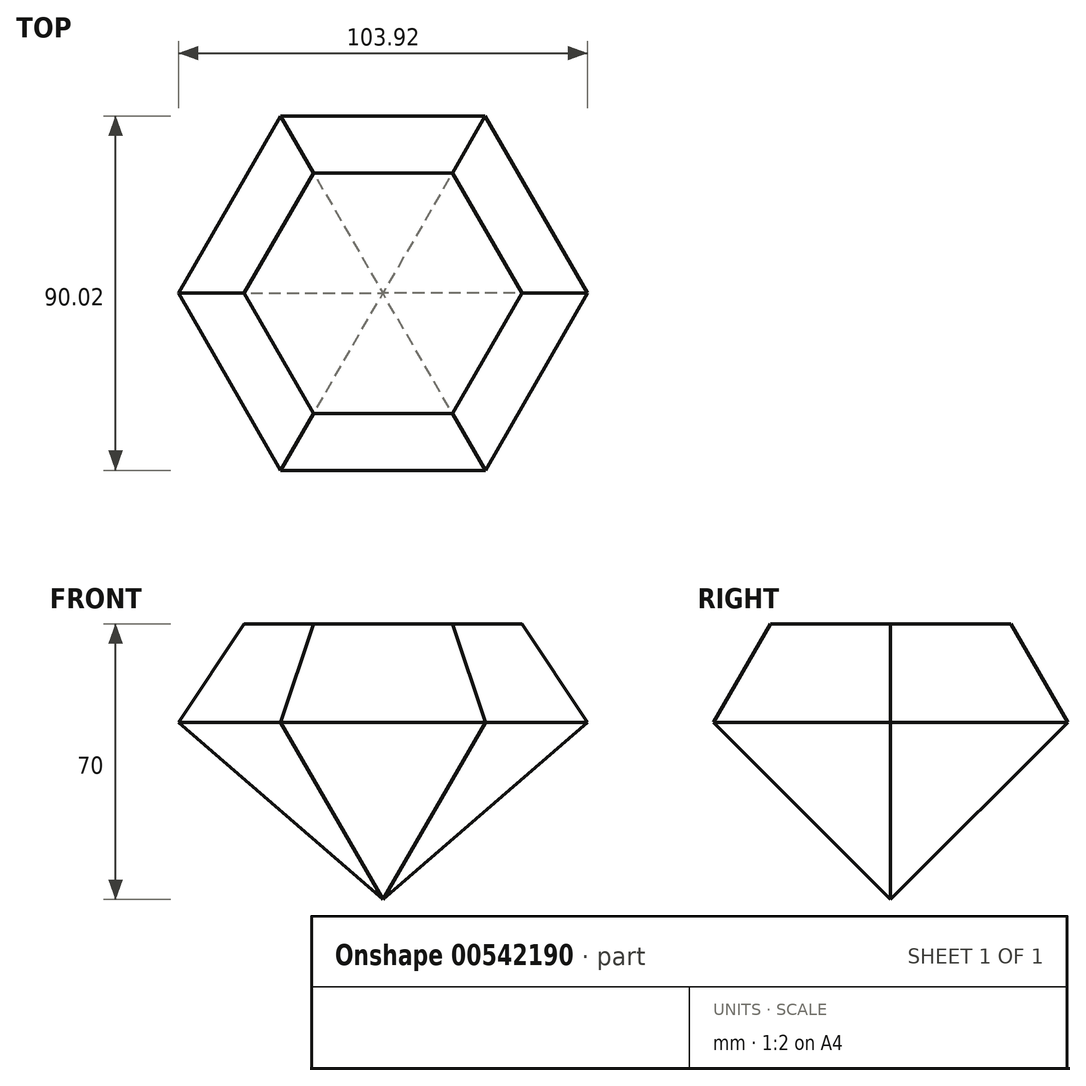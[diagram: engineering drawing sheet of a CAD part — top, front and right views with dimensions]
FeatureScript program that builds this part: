
annotation { "Feature Type Name" : "Feature", "Feature Type Description" : "" }
export const myFeature = defineFeature(function(context is Context, id is Id, definition is map)
    precondition{}
    {
        {
            var Q0;
            Q0=qCreatedBy(makeId("Top.planeOp"),FACE);
            var sketch = newSketch(context, id + "F0", { "sketchPlane" : qUnion([Q0])});
            skCircle(sketch, "E0.cCircle", {"center": v(0, 0) * mm, "radius": 51.96 * mm, "construction": true});
            skLineSegment(sketch, "E0.0", {"start": v(25.97, 45) * mm, "end": v(51.96, 0.01) * mm});
            skLineSegment(sketch, "E0.1", {"start": v(51.96, 0.01) * mm, "end": v(26, -45) * mm});
            skLineSegment(sketch, "E0.2", {"start": v(26, -45) * mm, "end": v(-25.97, -45) * mm});
            skLineSegment(sketch, "E0.3", {"start": v(-25.97, -45) * mm, "end": v(-51.96, -0.01) * mm});
            skLineSegment(sketch, "E0.4", {"start": v(-51.96, -0.01) * mm, "end": v(-26, 45) * mm});
            skLineSegment(sketch, "E0.5", {"start": v(-26, 45) * mm, "end": v(25.97, 45) * mm});
            skSolve(sketch);
        }
        {
            var Q0;
            Q0=makeQuery(id+"F0.imprint","IMPRINT",FACE,{"disambiguationData":[TD([[makeQuery(id+"F0.imprint","IMPRINT",EDGE,{"derivedFrom":sQuery(id+"F0.wireOp",EDGE,"E0.0")}),-1.0]])]});
            extrude(context, id + "F1", {"entities" : qUnion([Q0]), "depth" : 25 * mm, "offsetDistance" : 25 * mm, "hasDraft" : true, "draftAngle" : 30 * degree, "draftPullDirection" : true, "hasSecondDirection" : true, "secondDirectionOppositeDirection" : true, "secondDirectionDepth" : 50 * mm, "hasSecondDirectionDraft" : true, "secondDirectionDraftAngle" : 45 * degree, "secondDirectionDraftPullDirection" : true});
        }
    });
